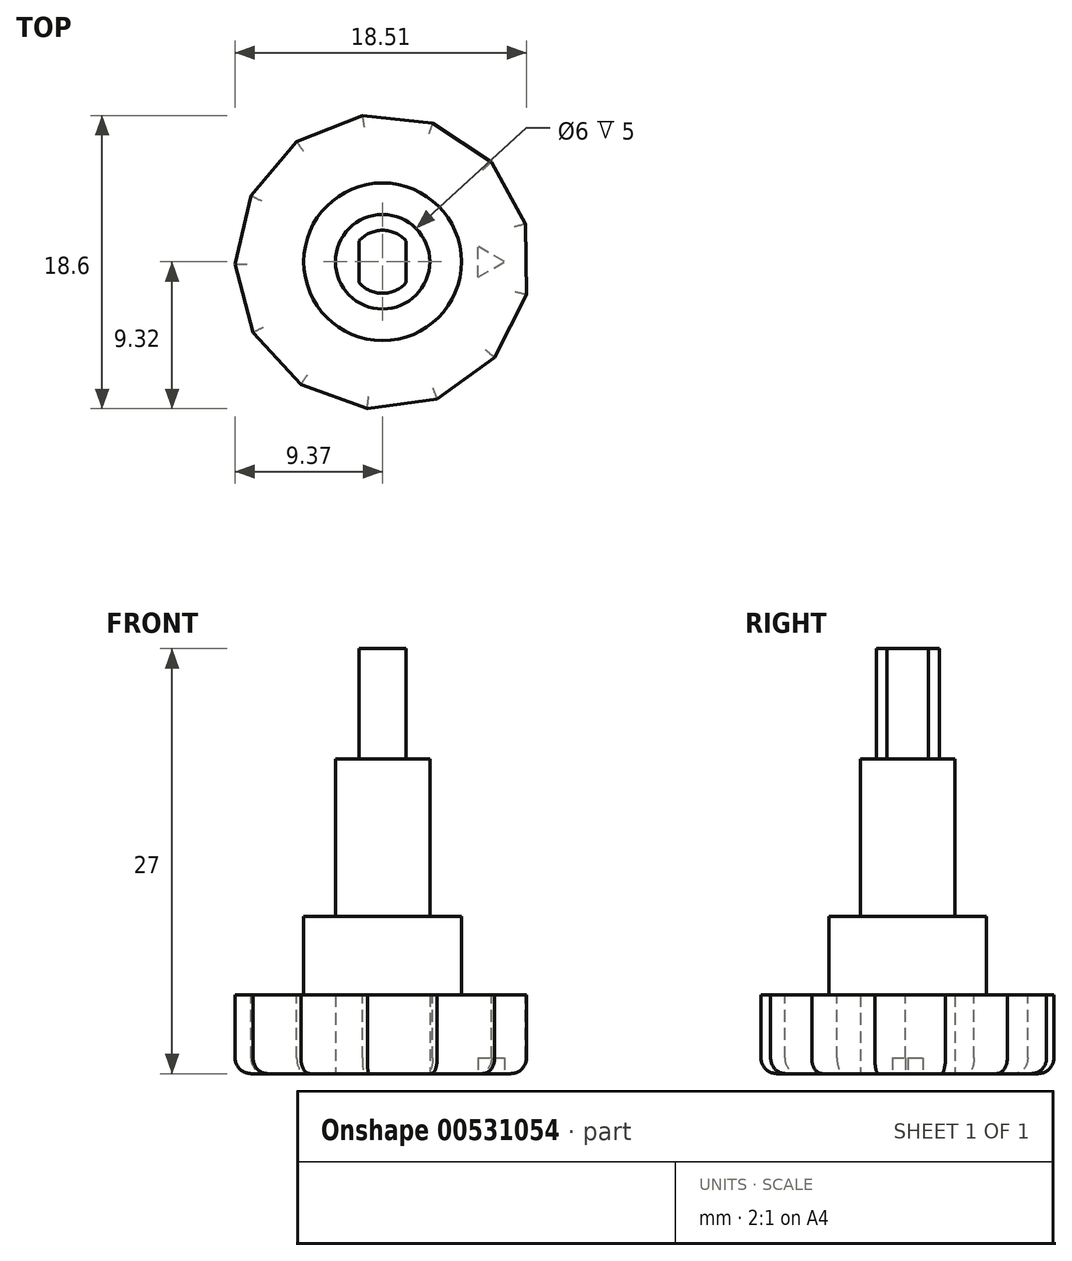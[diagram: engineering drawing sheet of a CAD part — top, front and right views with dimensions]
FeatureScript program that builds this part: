
annotation { "Feature Type Name" : "Feature", "Feature Type Description" : "" }
export const myFeature = defineFeature(function(context is Context, id is Id, definition is map)
    precondition{}
    {
        {
            var Q0;
            Q0=qCreatedBy(makeId("Top.planeOp"),FACE);
            var sketch = newSketch(context, id + "F0", { "sketchPlane" : qUnion([Q0])});
            skCircle(sketch, "E0", {"center": v(0, 0) * mm, "radius": 3 * mm});
            skSolve(sketch);
        }
        {
            var Q0;
            Q0=makeQuery(id+"F0.imprint","IMPRINT",FACE,{"disambiguationData":[TD([[makeQuery(id+"F0.imprint","IMPRINT",EDGE,{"derivedFrom":sQuery(id+"F0.wireOp",EDGE,"E0")}),1.0]])]});
            var Q1;
            Q1=sQuery(id+"F0.wireOp",EDGE,"E0");
            extrude(context, id + "F1", {"entities" : qUnion([Q0]), "surfaceEntities" : qUnion([Q1]), "depth" : 9 * mm, "offsetDistance" : 25 * mm});
        }
        {
            var Q0;
            Q0 = qSketchRegion(id + "F0", true);
            var Q1;
            Q1=makeQuery(id+"F1.opExtrude","CAP_FACE",FACE,{"disambiguationData":[OSD([sQuery(id+"F0.wireOp",EDGE,"E0")])],"isStart":false});
            extrude(context, id + "F2", {"entities" : qUnion([Q0, Q1]), "operationType" : NewBodyOperationType.ADD, "oppositeDirection" : true, "depth" : 6 * mm, "offsetDistance" : 25 * mm});
        }
        {
            var Q0;
            Q0=makeQuery(id+"F1.opExtrude","CAP_FACE",FACE,{"disambiguationData":[OSD([sQuery(id+"F0.wireOp",EDGE,"E0")])],"isStart":false});
            var sketch = newSketch(context, id + "F3", { "sketchPlane" : qUnion([Q0])});
            skCircle(sketch, "E1", {"center": v(0, 0) * mm, "radius": 2 * mm});
            skSolve(sketch);
        }
        {
            var Q0;
            Q0=makeQuery(id+"F3.imprint","IMPRINT",FACE,{"disambiguationData":[TD([[makeQuery(id+"F3.imprint","IMPRINT",EDGE,{"derivedFrom":sQuery(id+"F3.wireOp",EDGE,"E1")}),1.0]])]});
            extrude(context, id + "F4", {"entities" : qUnion([Q0]), "operationType" : NewBodyOperationType.ADD, "depth" : 7 * mm, "offsetDistance" : 25 * mm});
        }
        {
            var Q0;
            Q0=makeQuery(id+"F3.imprint","IMPRINT",FACE,{"disambiguationData":[TD([[makeQuery(id+"F3.imprint","IMPRINT",EDGE,{"derivedFrom":sQuery(id+"F3.wireOp",EDGE,"E1")}),-1.0]])]});
            extrude(context, id + "F5", {"entities" : qUnion([Q0]), "operationType" : NewBodyOperationType.REMOVE, "depth" : 7 * mm, "offsetDistance" : 25 * mm});
        }
        {
            var Q0;
            Q0=makeQuery(id+"F4.opExtrude","CAP_FACE",FACE,{"disambiguationData":[OSD([sQuery(id+"F3.wireOp",EDGE,"E1")])],"isStart":false});
            var sketch = newSketch(context, id + "F6", { "sketchPlane" : qUnion([Q0])});
            skLineSegment(sketch, "E2.left", {"start": v(-1.5, 2) * mm, "end": v(-1.5, -2) * mm});
            skLineSegment(sketch, "E2.right", {"start": v(1.5, 2) * mm, "end": v(1.5, -2) * mm});
            skPoint(sketch, "E2.middle", {"position": v(0, 0) * mm});
            skSolve(sketch);
        }
        {
            var Q0;
            {var subQ0=sQuery(id+"F6.wireOp",EDGE,"E2.left");var subQ1=makeQuery(id+"F4.opExtrude","CAP_EDGE",EDGE,{"disambiguationData":[OSD([sQuery(id+"F3.wireOp",EDGE,"E1")])],"isStart":false});var subQ2=makeQuery(id+"F6.imprint","INTERSECT",VERTEX,{"disambiguationData":[OD(0.0)],"derivedFrom":[subQ1,subQ0]});Q0=makeQuery(id+"F6.imprint","IMPRINT",FACE,{"disambiguationData":[TD([[makeQuery(id+"F6.imprint","IMPRINT",EDGE,{"disambiguationData":[TD([[subQ2,1.0]])],"derivedFrom":subQ0}),-1.0]])]});}
            var Q1;
            {var subQ0=sQuery(id+"F6.wireOp",EDGE,"E2.right");var subQ1=makeQuery(id+"F4.opExtrude","CAP_EDGE",EDGE,{"disambiguationData":[OSD([sQuery(id+"F3.wireOp",EDGE,"E1")])],"isStart":false});var subQ2=makeQuery(id+"F6.imprint","INTERSECT",VERTEX,{"disambiguationData":[OD(0.0)],"derivedFrom":[subQ1,subQ0]});Q1=makeQuery(id+"F6.imprint","IMPRINT",FACE,{"disambiguationData":[TD([[makeQuery(id+"F6.imprint","IMPRINT",EDGE,{"disambiguationData":[TD([[subQ2,1.0]])],"derivedFrom":subQ0}),1.0]])]});}
            var Q2;
            Q2 = qConstructionFilter(qBodyType(qCreatedBy(id + "F6" ,EDGE), BodyType.WIRE), ConstructionObject.NO);
            extrude(context, id + "F7", {"entities" : qUnion([Q0, Q1]), "operationType" : NewBodyOperationType.REMOVE, "surfaceEntities" : qUnion([Q2]), "oppositeDirection" : true, "depth" : 7 * mm, "offsetDistance" : 25 * mm});
        }
        {
            var Q0;
            {var subQ0=sQuery(id+"F0.wireOp",EDGE,"E0");Q0=makeQuery(id+"F2.opExtrude","CAP_FACE",FACE,{"disambiguationData":[OSD([subQ0]),TDD([makeQuery(id+"F0.imprint","IMPRINT",EDGE,{"derivedFrom":subQ0})])],"isStart":false});}
            var sketch = newSketch(context, id + "F8", { "sketchPlane" : qUnion([Q0])});
            skCircle(sketch, "E3.cCircle", {"center": v(0, 0) * mm, "radius": 9.37 * mm, "construction": true});
            skLineSegment(sketch, "E3.0", {"start": v(-8.22, 4.5) * mm, "end": v(-5.2, 7.8) * mm});
            skLineSegment(sketch, "E3.1", {"start": v(-5.2, 7.8) * mm, "end": v(-0.97, 9.32) * mm});
            skLineSegment(sketch, "E3.2", {"start": v(-0.97, 9.32) * mm, "end": v(3.47, 8.7) * mm});
            skLineSegment(sketch, "E3.3", {"start": v(3.47, 8.7) * mm, "end": v(7.12, 6.1) * mm});
            skLineSegment(sketch, "E3.4", {"start": v(7.12, 6.1) * mm, "end": v(9.14, 2.09) * mm});
            skLineSegment(sketch, "E3.5", {"start": v(9.14, 2.09) * mm, "end": v(9.06, -2.4) * mm});
            skLineSegment(sketch, "E3.6", {"start": v(9.06, -2.4) * mm, "end": v(6.9, -6.33) * mm});
            skLineSegment(sketch, "E3.7", {"start": v(6.9, -6.33) * mm, "end": v(3.17, -8.82) * mm});
            skLineSegment(sketch, "E3.8", {"start": v(3.17, -8.82) * mm, "end": v(-1.29, -9.28) * mm});
            skLineSegment(sketch, "E3.9", {"start": v(-1.29, -9.28) * mm, "end": v(-5.45, -7.62) * mm});
            skLineSegment(sketch, "E3.10", {"start": v(-5.45, -7.62) * mm, "end": v(-8.37, -4.21) * mm});
            skLineSegment(sketch, "E3.11", {"start": v(-8.37, -4.21) * mm, "end": v(-9.37, 0.16) * mm});
            skLineSegment(sketch, "E3.12", {"start": v(-9.37, 0.16) * mm, "end": v(-8.22, 4.5) * mm});
            skCircle(sketch, "E4", {"center": v(0, 0) * mm, "radius": 5 * mm});
            skSolve(sketch);
        }
        {
            var Q0;
            Q0 = qSketchRegion(id + "F8", true);
            extrude(context, id + "F9", {"entities" : qUnion([Q0]), "operationType" : NewBodyOperationType.ADD, "depth" : 5 * mm, "offsetDistance" : 25 * mm});
        }
        {
            var Q0;
            Q0=makeQuery(id+"F9.opExtrude","CAP_EDGE",EDGE,{"disambiguationData":[OSD([sQuery(id+"F8.wireOp",EDGE,"E3.0")])],"isStart":false});
            var Q1;
            Q1=makeQuery(id+"F9.opExtrude","CAP_EDGE",EDGE,{"disambiguationData":[OSD([sQuery(id+"F8.wireOp",EDGE,"E3.1")])],"isStart":false});
            var Q2;
            Q2=makeQuery(id+"F9.opExtrude","CAP_EDGE",EDGE,{"disambiguationData":[OSD([sQuery(id+"F8.wireOp",EDGE,"E3.2")])],"isStart":false});
            var Q3;
            Q3=makeQuery(id+"F9.opExtrude","CAP_EDGE",EDGE,{"disambiguationData":[OSD([sQuery(id+"F8.wireOp",EDGE,"E3.3")])],"isStart":false});
            var Q4;
            Q4=makeQuery(id+"F9.opExtrude","CAP_EDGE",EDGE,{"disambiguationData":[OSD([sQuery(id+"F8.wireOp",EDGE,"E3.4")])],"isStart":false});
            var Q5;
            Q5=makeQuery(id+"F9.opExtrude","CAP_EDGE",EDGE,{"disambiguationData":[OSD([sQuery(id+"F8.wireOp",EDGE,"E3.5")])],"isStart":false});
            var Q6;
            Q6=makeQuery(id+"F9.opExtrude","CAP_EDGE",EDGE,{"disambiguationData":[OSD([sQuery(id+"F8.wireOp",EDGE,"E3.6")])],"isStart":false});
            var Q7;
            Q7=makeQuery(id+"F9.opExtrude","CAP_EDGE",EDGE,{"disambiguationData":[OSD([sQuery(id+"F8.wireOp",EDGE,"E3.7")])],"isStart":false});
            var Q8;
            Q8=makeQuery(id+"F9.opExtrude","CAP_EDGE",EDGE,{"disambiguationData":[OSD([sQuery(id+"F8.wireOp",EDGE,"E3.8")])],"isStart":false});
            var Q9;
            Q9=makeQuery(id+"F9.opExtrude","CAP_EDGE",EDGE,{"disambiguationData":[OSD([sQuery(id+"F8.wireOp",EDGE,"E3.9")])],"isStart":false});
            var Q10;
            Q10=makeQuery(id+"F9.opExtrude","CAP_EDGE",EDGE,{"disambiguationData":[OSD([sQuery(id+"F8.wireOp",EDGE,"E3.10")])],"isStart":false});
            var Q11;
            Q11=makeQuery(id+"F9.opExtrude","CAP_EDGE",EDGE,{"disambiguationData":[OSD([sQuery(id+"F8.wireOp",EDGE,"E3.11")])],"isStart":false});
            var Q12;
            Q12=makeQuery(id+"F9.opExtrude","CAP_EDGE",EDGE,{"disambiguationData":[OSD([sQuery(id+"F8.wireOp",EDGE,"E3.12")])],"isStart":false});
            fillet(context, id + "F10", {"entities" : qUnion([Q0, Q1, Q2, Q3, Q4, Q5, Q6, Q7, Q8, Q9, Q10, Q11, Q12]), "radius" : 1 * mm, "tangentPropagation" : true, "allowEdgeOverflow" : false});
        }
        {
            var Q0;
            Q0=makeQuery(id+"F9.opExtrude","CAP_FACE",FACE,{"disambiguationData":[OSD([sQuery(id+"F8.wireOp",EDGE,"E3.0"),sQuery(id+"F8.wireOp",EDGE,"E3.1"),sQuery(id+"F8.wireOp",EDGE,"E3.2"),sQuery(id+"F8.wireOp",EDGE,"E3.3"),sQuery(id+"F8.wireOp",EDGE,"E3.4"),sQuery(id+"F8.wireOp",EDGE,"E3.5"),sQuery(id+"F8.wireOp",EDGE,"E3.6"),sQuery(id+"F8.wireOp",EDGE,"E3.7"),sQuery(id+"F8.wireOp",EDGE,"E3.8"),sQuery(id+"F8.wireOp",EDGE,"E3.9"),sQuery(id+"F8.wireOp",EDGE,"E3.10"),sQuery(id+"F8.wireOp",EDGE,"E3.11"),sQuery(id+"F8.wireOp",EDGE,"E3.12")])],"isStart":false});
            var sketch = newSketch(context, id + "F11", { "sketchPlane" : qUnion([Q0])});
            skPoint(sketch, "E5.middle", {"position": v(4.31, 0) * mm});
            skLineSegment(sketch, "E6", {"start": v(6.07, 0.98) * mm, "end": v(7.73, 0) * mm});
            skLineSegment(sketch, "E7", {"start": v(7.73, 0) * mm, "end": v(6.07, -0.98) * mm});
            skLineSegment(sketch, "E8", {"start": v(6.07, 0.98) * mm, "end": v(6.07, -0.98) * mm});
            skSolve(sketch);
        }
        {
            var Q0;
            Q0=makeQuery(id+"F8.imprint","IMPRINT",FACE,{"disambiguationData":[TD([[makeQuery(id+"F8.imprint","IMPRINT",EDGE,{"derivedFrom":sQuery(id+"F8.wireOp",EDGE,"E4")}),1.0]])]});
            extrude(context, id + "F12", {"entities" : qUnion([Q0]), "operationType" : NewBodyOperationType.ADD, "oppositeDirection" : true, "depth" : 5 * mm, "offsetDistance" : 25 * mm, "hasSecondDirection" : true, "secondDirectionOppositeDirection" : false, "secondDirectionDepth" : 5 * mm});
        }
        {
            var Q0;
            Q0=makeQuery(id+"F11.imprint","IMPRINT",FACE,{"disambiguationData":[TD([[makeQuery(id+"F11.imprint","IMPRINT",EDGE,{"derivedFrom":sQuery(id+"F11.wireOp",EDGE,"E6")}),-1.0]])]});
            extrude(context, id + "F13", {"entities" : qUnion([Q0]), "operationType" : NewBodyOperationType.REMOVE, "oppositeDirection" : true, "depth" : 1 * mm, "offsetDistance" : 25 * mm});
        }
    });
